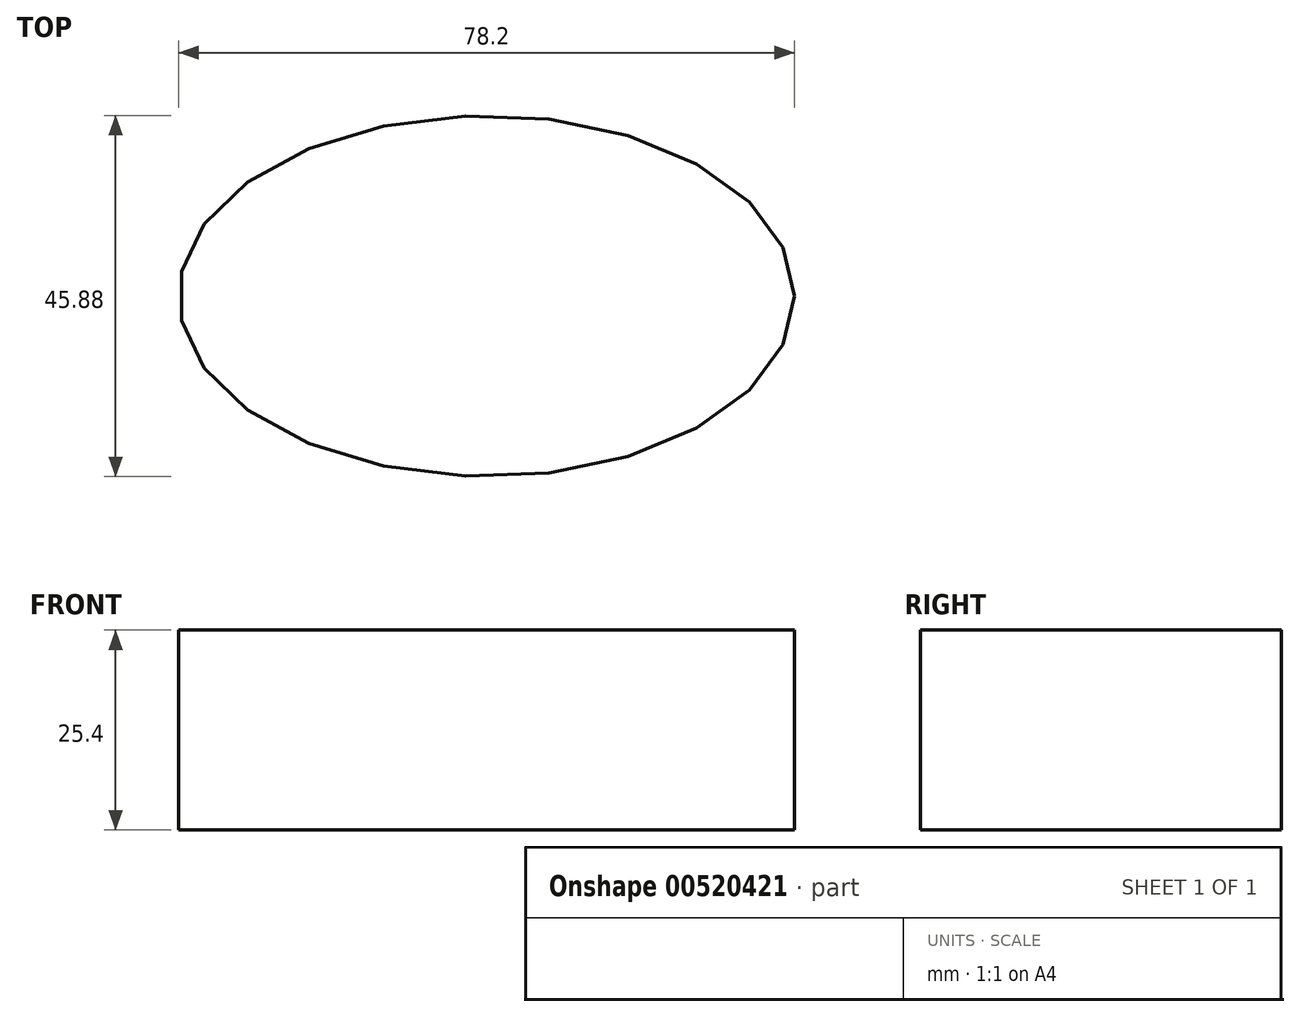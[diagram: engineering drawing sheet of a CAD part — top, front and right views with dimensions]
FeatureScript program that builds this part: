
annotation { "Feature Type Name" : "Feature", "Feature Type Description" : "" }
export const myFeature = defineFeature(function(context is Context, id is Id, definition is map)
    precondition{}
    {
        {
            var Q0;
            Q0=qCreatedBy(makeId("Top.planeOp"),FACE);
            var sketch = newSketch(context, id + "F0", { "sketchPlane" : qUnion([Q0])});
            skEllipse(sketch, "E0", {"center": v(0, 0) * mm, "majorRadius": 39.1 * mm, "minorRadius": 22.94 * mm, "majorAxis": v(1, 0)});
            skSolve(sketch);
        }
        {
            var Q0;
            Q0 = qSketchRegion(id + "F0", true);
            extrude(context, id + "F1", {"entities" : qUnion([Q0]), "depth" : 25.4 * mm, "offsetDistance" : 25.4 * mm});
        }
    });
